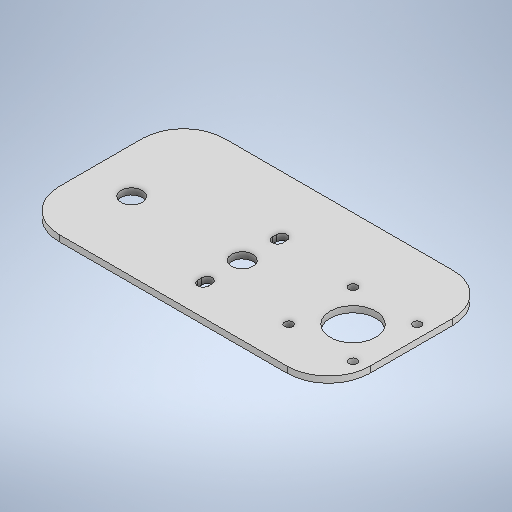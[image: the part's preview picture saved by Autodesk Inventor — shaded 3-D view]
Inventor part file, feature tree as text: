
AUTODESK INVENTOR PART (.ipt)
format: ipt  version: 2025.2 (Build 292293000, 293)  size: 293,888 bytes
history: native  units: mm
features: extrude x3, sketch x3, fillet x1
ambient origin geometry x8: Origin, YZ Plane, XZ Plane, XY Plane, X Axis, Y Axis, Z Axis, Center Point
bodies: Solid1 (feature_tree)
feature tree (7):
  extrude  "Extrusion1"  Depth=80.0mm
  extrude  "Extrusion4"  Depth=3.0mm
  extrude  "Extrusion6"  Depth=150.0mm
  fillet  "Fillet1"  Radius=43.2mm
  sketch  "Sketch1"  dims[d0=150.0mm d1=80.0mm]
  sketch  "Sketch5"  dims[d2=3.0mm d3=0.0mm d26=25.0mm]
  sketch  "Sketch6"  dims[d36=0.0mm d37=0.0mm d49=150.0mm d50=43.2mm d51=43.2mm d52=22.0mm d53=31.0mm d54=31.0mm d55=4.0mm d56=4.0mm d57=4.0mm d58=4.0mm d59=25.0mm d60=43.2mm d61=43.2mm d62=43.2mm d63=10.2mm d64=43.2mm d65=53.4mm d66=10.2mm d67=0.0mm d68=0.0mm d69=38.0mm d70=5.0mm d71=2.0mm d72=5.0mm d73=5.0mm d74=2.0mm d75=5.0mm d87=20.0mm d27=0.872665mm d28=0.5mm d29=0.872665mm]
